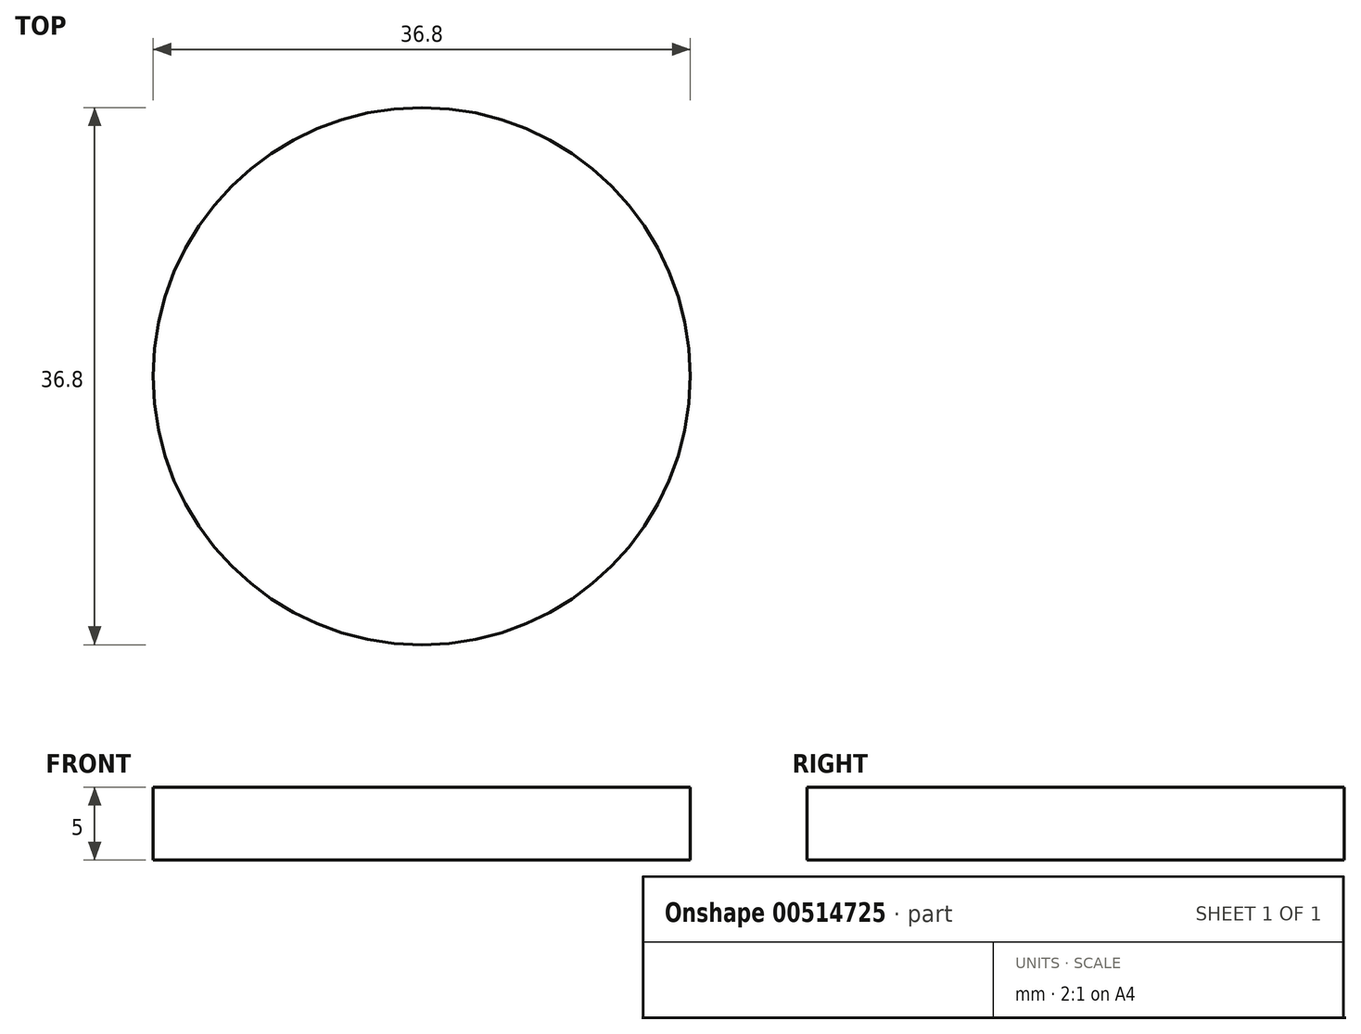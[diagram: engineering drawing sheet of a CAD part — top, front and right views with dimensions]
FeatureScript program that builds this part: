
annotation { "Feature Type Name" : "Feature", "Feature Type Description" : "" }
export const myFeature = defineFeature(function(context is Context, id is Id, definition is map)
    precondition{}
    {
        {
            var Q0;
            Q0=qCreatedBy(makeId("Top.planeOp"),FACE);
            var sketch = newSketch(context, id + "F0", { "sketchPlane" : qUnion([Q0])});
            skCircle(sketch, "E0", {"center": v(0, 0) * mm, "radius": 18.4 * mm});
            skSolve(sketch);
        }
        {
            var Q0;
            Q0 = qSketchRegion(id + "F0", true);
            extrude(context, id + "F1", {"entities" : qUnion([Q0]), "depth" : 5 * mm, "offsetDistance" : 25 * mm});
        }
    });
